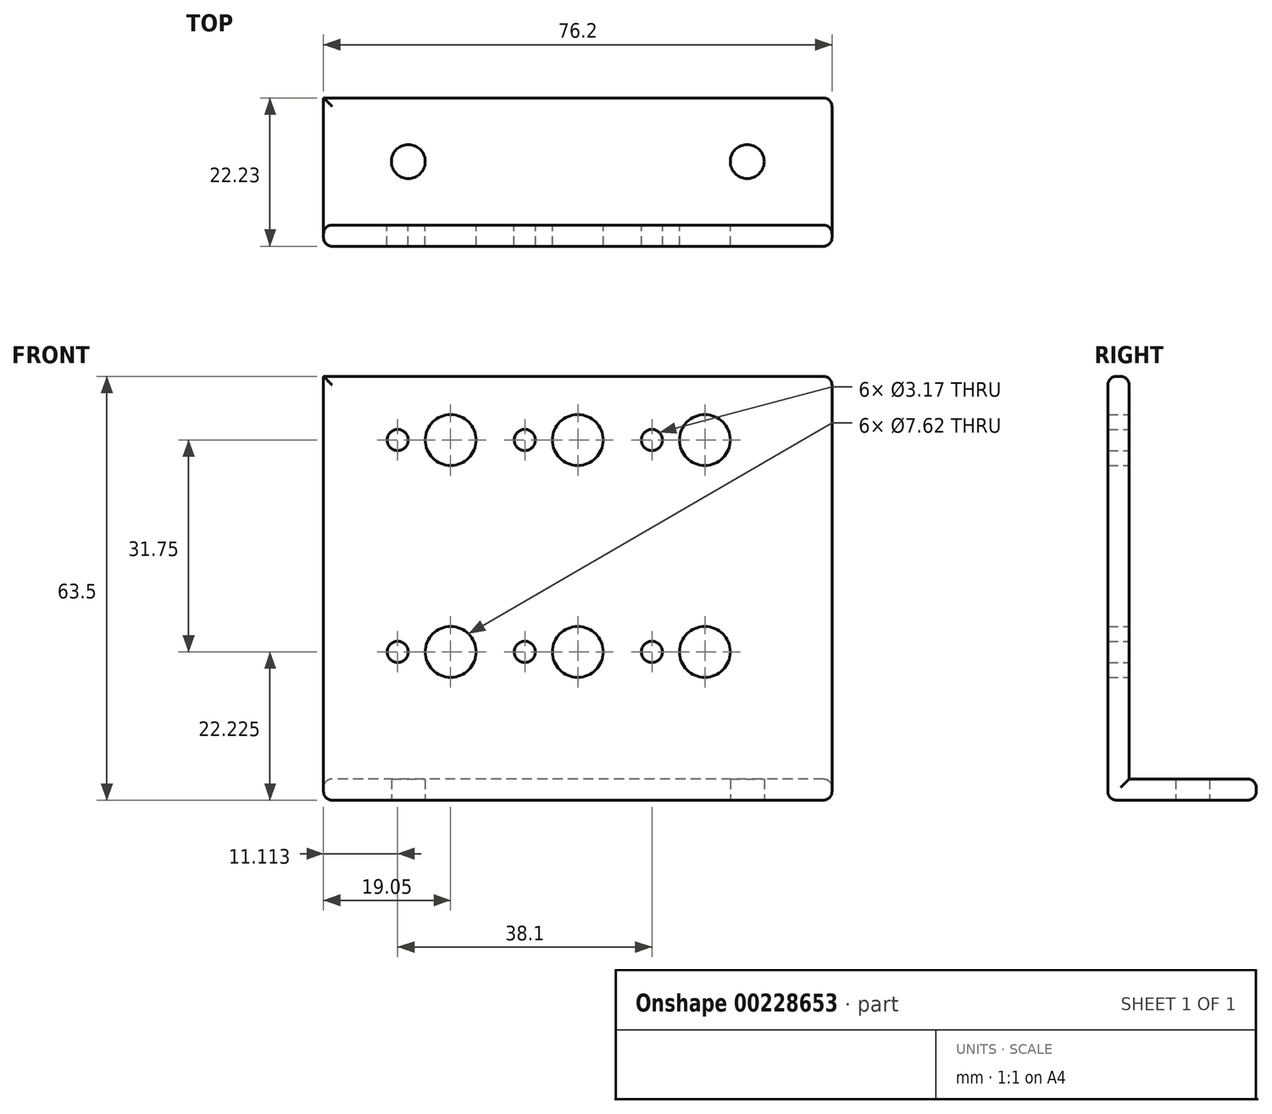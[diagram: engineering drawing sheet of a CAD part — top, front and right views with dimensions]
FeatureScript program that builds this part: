
annotation { "Feature Type Name" : "Feature", "Feature Type Description" : "" }
export const myFeature = defineFeature(function(context is Context, id is Id, definition is map)
    precondition{}
    {
        {
            var Q0;
            Q0=qCreatedBy(makeId("Front.planeOp"),FACE);
            var sketch = newSketch(context, id + "F0", { "sketchPlane" : qUnion([Q0])});
            skLineSegment(sketch, "E0", {"start": v(-32.74, 28.58) * mm, "end": v(32.61, 28.58) * mm, "construction": true});
            skLineSegment(sketch, "E1", {"start": v(-32.74, -3.17) * mm, "end": v(32.61, -3.17) * mm, "construction": true});
            skLineSegment(sketch, "E2", {"start": v(0, 42.48) * mm, "end": v(0, -31.73) * mm, "construction": true});
            skLineSegment(sketch, "E3", {"start": v(19.05, 21.95) * mm, "end": v(19.05, -21.33) * mm, "construction": true});
            skLineSegment(sketch, "E4", {"start": v(-19.05, 21.58) * mm, "end": v(-19.05, -21.7) * mm, "construction": true});
            skCircle(sketch, "E5", {"center": v(-19.05, 28.58) * mm, "radius": 3.81 * mm});
            skCircle(sketch, "E6", {"center": v(0, 28.58) * mm, "radius": 3.81 * mm});
            skCircle(sketch, "E7", {"center": v(19.05, 28.58) * mm, "radius": 3.81 * mm});
            skCircle(sketch, "E8", {"center": v(-19.05, -3.17) * mm, "radius": 3.81 * mm});
            skCircle(sketch, "E9", {"center": v(0, -3.17) * mm, "radius": 3.81 * mm});
            skCircle(sketch, "E10", {"center": v(19.05, -3.17) * mm, "radius": 3.81 * mm});
            skLineSegment(sketch, "E11.bottom", {"start": v(38.1, 38.1) * mm, "end": v(-38.1, 38.1) * mm});
            skLineSegment(sketch, "E11.top", {"start": v(38.1, -25.4) * mm, "end": v(-38.1, -25.4) * mm});
            skLineSegment(sketch, "E11.left", {"start": v(38.1, 38.1) * mm, "end": v(38.1, -25.4) * mm});
            skLineSegment(sketch, "E11.right", {"start": v(-38.1, 38.1) * mm, "end": v(-38.1, -25.4) * mm});
            skPoint(sketch, "E12", {"position": v(0, 38.1) * mm});
            skCircle(sketch, "E13", {"center": v(-26.99, 28.58) * mm, "radius": 1.59 * mm});
            skCircle(sketch, "E14", {"center": v(-7.94, 28.58) * mm, "radius": 1.59 * mm});
            skCircle(sketch, "E15", {"center": v(11.11, 28.58) * mm, "radius": 1.59 * mm});
            skCircle(sketch, "E16", {"center": v(-26.99, -3.17) * mm, "radius": 1.59 * mm});
            skCircle(sketch, "E17", {"center": v(-7.94, -3.17) * mm, "radius": 1.59 * mm});
            skCircle(sketch, "E18", {"center": v(11.11, -3.17) * mm, "radius": 1.59 * mm});
            skSolve(sketch);
        }
        {
            var Q0;
            Q0 = qSketchRegion(id + "F0", true);
            extrude(context, id + "F1", {"entities" : qUnion([Q0]), "depth" : 3.17 * mm});
        }
        {
            var Q0;
            Q0=qCreatedBy(makeId("Right.planeOp"),FACE);
            var sketch = newSketch(context, id + "F2", { "sketchPlane" : qUnion([Q0])});
            skLineSegment(sketch, "E19.bottom", {"start": v(0, -25.4) * mm, "end": v(19.05, -25.4) * mm});
            skLineSegment(sketch, "E19.top", {"start": v(0, -22.22) * mm, "end": v(19.05, -22.22) * mm});
            skLineSegment(sketch, "E19.left", {"start": v(0, -25.4) * mm, "end": v(0, -22.22) * mm});
            skLineSegment(sketch, "E19.right", {"start": v(19.05, -25.4) * mm, "end": v(19.05, -22.22) * mm});
            skSolve(sketch);
        }
        {
            var Q0;
            Q0=makeQuery(id+"FII0WPnmGI6h7Gj_1.boolean.opBoolean","MERGE",FACE,{"derivedFrom":[makeQuery(id+"F1.opExtrude","SWEPT_FACE",FACE,{"disambiguationData":[OSD([sQuery(id+"F0.wireOp",EDGE,"E11.top")])]}),makeQuery(id+"FII0WPnmGI6h7Gj_1.opExtrude","SWEPT_FACE",FACE,{"disambiguationData":[OSD([sQuery(id+"F2.wireOp",EDGE,"E19.bottom")])]})]});
            var sketch = newSketch(context, id + "F3", { "sketchPlane" : qUnion([Q0])});
            skCircle(sketch, "E20", {"center": v(-25.4, -9.53) * mm, "radius": 2.54 * mm});
            skCircle(sketch, "E21", {"center": v(25.4, -9.53) * mm, "radius": 2.54 * mm});
            skLineSegment(sketch, "E22", {"start": v(-51.92, -9.53) * mm, "end": v(40.9, -9.53) * mm, "construction": true});
            skLineSegment(sketch, "E23.bottom", {"start": v(38.1, -19.05) * mm, "end": v(-38.1, -19.05) * mm});
            skLineSegment(sketch, "E23.top", {"start": v(38.1, 0) * mm, "end": v(-38.1, 0) * mm});
            skLineSegment(sketch, "E23.left", {"start": v(38.1, -19.05) * mm, "end": v(38.1, 0) * mm});
            skLineSegment(sketch, "E23.right", {"start": v(-38.1, -19.05) * mm, "end": v(-38.1, 0) * mm});
            skPoint(sketch, "E23.middle", {"position": v(0, -9.53) * mm});
            skSolve(sketch);
        }
        {
            var Q0;
            Q0=makeQuery(id+"F3.imprint","IMPRINT",FACE,{"disambiguationData":[TD([[makeQuery(id+"F3.imprint","IMPRINT",EDGE,{"derivedFrom":sQuery(id+"F3.wireOp",EDGE,"E20")}),-1.0]])]});
            extrude(context, id + "F4", {"entities" : qUnion([Q0]), "operationType" : NewBodyOperationType.ADD, "oppositeDirection" : true, "depth" : 3.17 * mm});
        }
        {
            var Q0;
            Q0=makeQuery(id+"F1.opExtrude","CAP_EDGE",EDGE,{"disambiguationData":[OSD([sQuery(id+"F0.wireOp",EDGE,"E11.left")])],"isStart":false});
            var Q1;
            Q1=makeQuery(id+"F1.opExtrude","CAP_EDGE",EDGE,{"disambiguationData":[OSD([sQuery(id+"F0.wireOp",EDGE,"E11.left")])],"isStart":true});
            var Q2;
            Q2=makeQuery(id+"F1.opExtrude","CAP_EDGE",EDGE,{"disambiguationData":[OSD([sQuery(id+"F0.wireOp",EDGE,"E11.right")])],"isStart":false});
            var Q3;
            Q3=makeQuery(id+"F1.opExtrude","CAP_EDGE",EDGE,{"disambiguationData":[OSD([sQuery(id+"F0.wireOp",EDGE,"E11.right")])],"isStart":true});
            var Q4;
            Q4=makeQuery(id+"F1.opExtrude","CAP_EDGE",EDGE,{"disambiguationData":[OSD([sQuery(id+"F0.wireOp",EDGE,"E11.bottom")])],"isStart":true});
            var Q5;
            Q5=makeQuery(id+"F1.opExtrude","CAP_EDGE",EDGE,{"disambiguationData":[OSD([sQuery(id+"F0.wireOp",EDGE,"E11.bottom")])],"isStart":false});
            var Q6;
            Q6=makeQuery(id+"F4.opExtrude","CAP_EDGE",EDGE,{"disambiguationData":[OSD([sQuery(id+"F3.wireOp",EDGE,"E23.top")])],"isStart":false});
            var Q7;
            Q7=makeQuery(id+"F4.opExtrude","CAP_EDGE",EDGE,{"disambiguationData":[OSD([sQuery(id+"F3.wireOp",EDGE,"E23.bottom")])],"isStart":false});
            var Q8;
            Q8=makeQuery(id+"F4.boolean.opBoolean","MERGE",FACE,{"derivedFrom":[makeQuery(id+"F1.opExtrude","SWEPT_FACE",FACE,{"disambiguationData":[OSD([sQuery(id+"F0.wireOp",EDGE,"E11.left")])]}),makeQuery(id+"F4.opExtrude","SWEPT_FACE",FACE,{"disambiguationData":[OSD([sQuery(id+"F3.wireOp",EDGE,"E23.left")])]})]});
            var Q9;
            Q9=makeQuery(id+"F4.opExtrude","CAP_EDGE",EDGE,{"disambiguationData":[OSD([sQuery(id+"F3.wireOp",EDGE,"E23.bottom")])],"isStart":true});
            var Q10;
            Q10=makeQuery(id+"F4.boolean.opBoolean","MERGE",EDGE,{"derivedFrom":[makeQuery(id+"F1.opExtrude","SWEPT_EDGE",EDGE,{"disambiguationData":[OSD([sQuery(id+"F0.wireOp",EDGE,"E11.top"),sQuery(id+"F0.wireOp",EDGE,"E11.right")])]}),makeQuery(id+"F4.opExtrude","CAP_EDGE",EDGE,{"disambiguationData":[OSD([sQuery(id+"F3.wireOp",EDGE,"E23.right")])],"isStart":true})]});
            var Q11;
            Q11=makeQuery(id+"F1.opExtrude","CAP_EDGE",EDGE,{"disambiguationData":[OSD([sQuery(id+"F0.wireOp",EDGE,"E11.top")])],"isStart":false});
            var Q12;
            Q12=makeQuery(id+"F4.opExtrude","CAP_EDGE",EDGE,{"disambiguationData":[OSD([sQuery(id+"F3.wireOp",EDGE,"E23.right")])],"isStart":false});
            fillet(context, id + "F5", {"entities" : qUnion([Q0, Q1, Q2, Q3, Q4, Q5, Q6, Q7, Q8, Q9, Q10, Q11, Q12]), "radius" : 1.27 * mm, "tangentPropagation" : true, "allowEdgeOverflow" : false});
        }
    });
